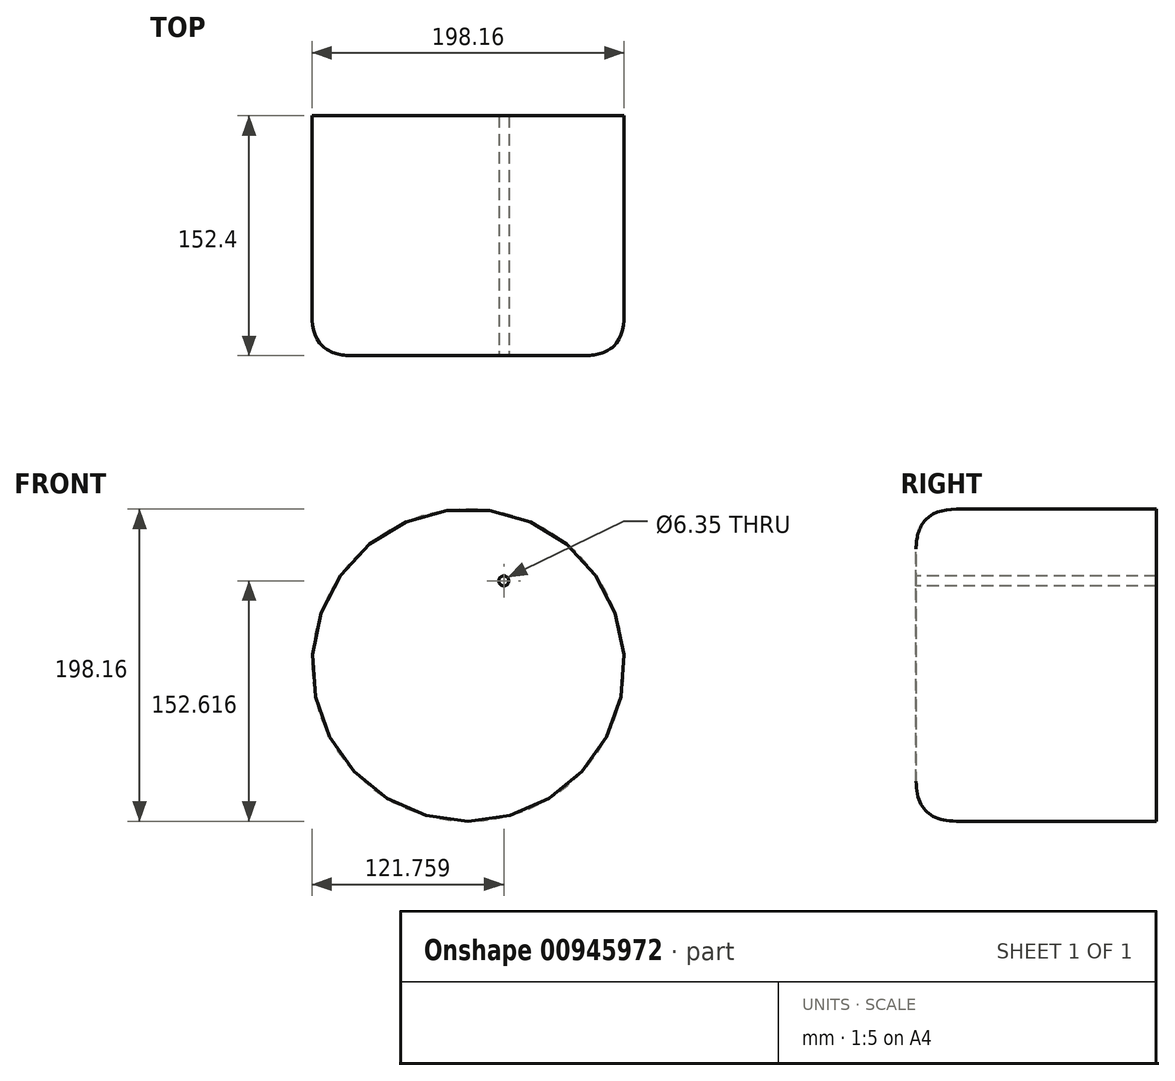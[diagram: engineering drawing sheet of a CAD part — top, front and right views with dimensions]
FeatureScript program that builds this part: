
annotation { "Feature Type Name" : "Feature", "Feature Type Description" : "" }
export const myFeature = defineFeature(function(context is Context, id is Id, definition is map)
    precondition{}
    {
        {
            var Q0;
            Q0=qCreatedBy(makeId("Front.planeOp"),FACE);
            var sketch = newSketch(context, id + "F0", { "sketchPlane" : qUnion([Q0])});
            skCircle(sketch, "E0", {"center": v(0, 0) * mm, "radius": 99.08 * mm});
            skSolve(sketch);
        }
        {
            var Q0;
            Q0 = qSketchRegion(id + "F0", true);
            extrude(context, id + "F1", {"entities" : qUnion([Q0]), "depth" : 152.4 * mm, "offsetDistance" : 25.4 * mm});
        }
        {
            var Q0;
            Q0=makeQuery(id+"F1.opExtrude","CAP_FACE",FACE,{"disambiguationData":[OSD([sQuery(id+"F0.wireOp",EDGE,"E0")])],"isStart":false});
            var sketch = newSketch(context, id + "F2", { "sketchPlane" : qUnion([Q0])});
            skPoint(sketch, "E1", {"position": v(22.11, 21.69) * mm});
            skPoint(sketch, "E2", {"position": v(22.68, 53.54) * mm});
            skSolve(sketch);
        }
        {
            var Q0;
            Q0=sQuery(id+"F2.wireOp",VERTEX,"E2");
            var Q1;
            Q1=makeQuery(id+"F1.opExtrude","SWEPT_BODY",BODY,{"disambiguationData":[OSD([sQuery(id+"F0.wireOp",EDGE,"E0")])]});
            hole(context, id + "F3", {"style" : HoleStyle.SIMPLE, "endStyle" : HoleEndStyle.THROUGH, "holeDiameter" : 6.35 * mm, "majorDiameter" : 6.35 * mm, "isTappedThrough" : true, "tappedDepth" : 12.7 * mm, "tapClearance" : 3, "locations" : qUnion([Q0]), "scope" : qUnion([Q1])});
        }
        {
            var Q0;
            Q0=makeQuery(id+"F1.opExtrude","CAP_EDGE",EDGE,{"disambiguationData":[OSD([sQuery(id+"F0.wireOp",EDGE,"E0")])],"isStart":false});
            fillet(context, id + "F4", {"entities" : qUnion([Q0]), "radius" : 25.4 * mm, "tangentPropagation" : true, "rho" : 0.5, "crossSection" : FilletCrossSection.CONIC, "allowEdgeOverflow" : false});
        }
    });
